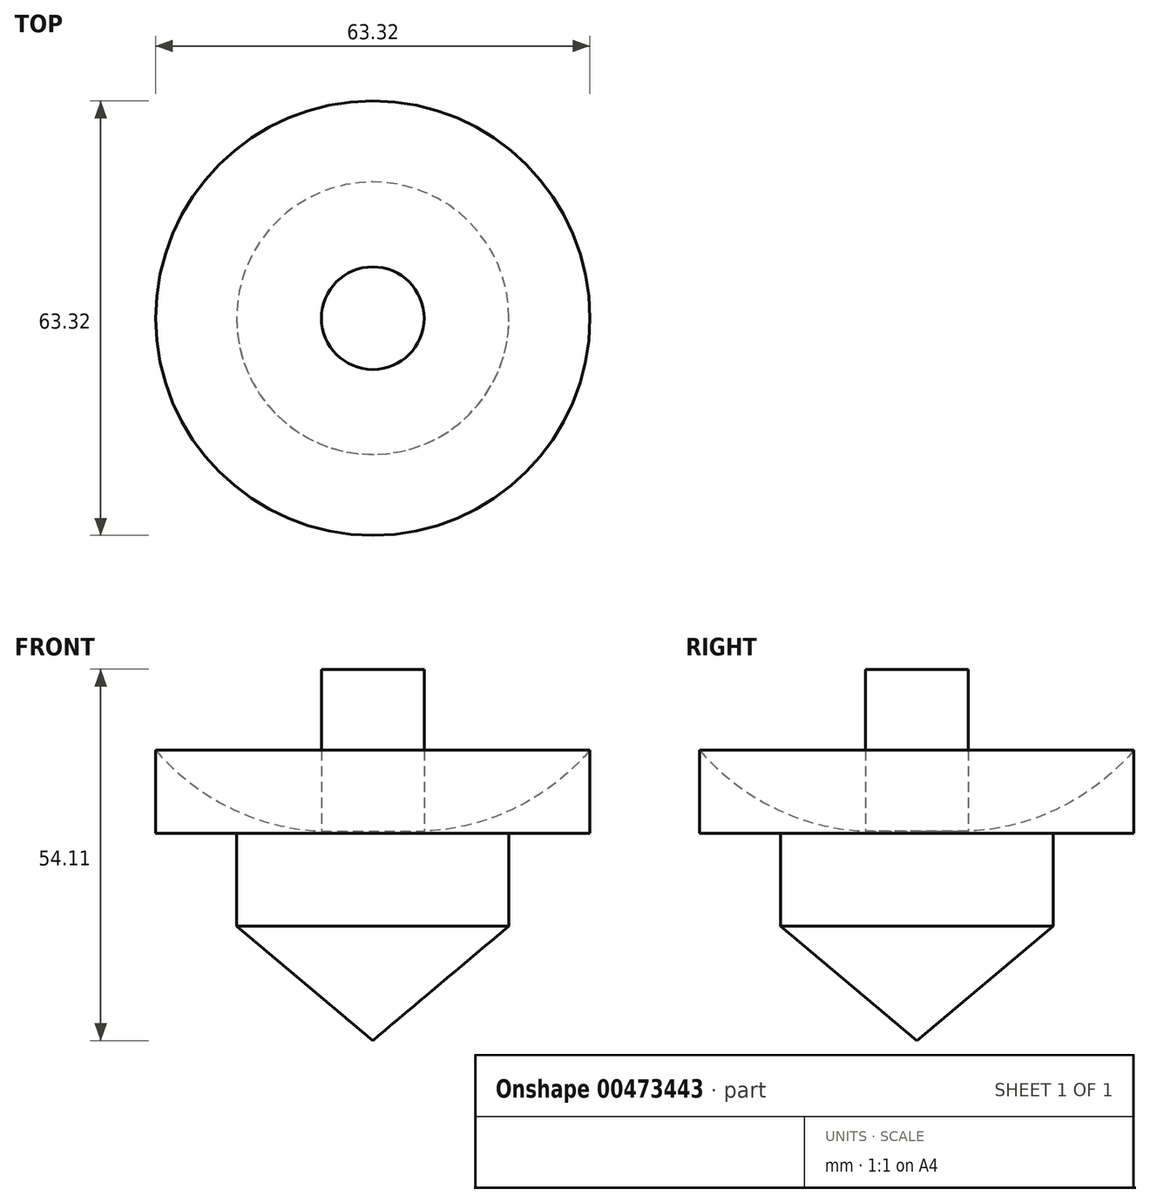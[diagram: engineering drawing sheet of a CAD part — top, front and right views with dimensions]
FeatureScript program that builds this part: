
annotation { "Feature Type Name" : "Feature", "Feature Type Description" : "" }
export const myFeature = defineFeature(function(context is Context, id is Id, definition is map)
    precondition{}
    {
        {
            var Q0;
            Q0=qCreatedBy(makeId("Front.planeOp"),FACE);
            var sketch = newSketch(context, id + "F0", { "sketchPlane" : qUnion([Q0])});
            skLineSegment(sketch, "E0", {"start": v(0, 0) * mm, "end": v(19.86, 16.7) * mm});
            skLineSegment(sketch, "E1", {"start": v(19.86, 16.7) * mm, "end": v(19.86, 30.22) * mm});
            skLineSegment(sketch, "E2", {"start": v(19.86, 30.22) * mm, "end": v(31.66, 30.22) * mm});
            skLineSegment(sketch, "E3", {"start": v(31.66, 30.22) * mm, "end": v(31.66, 42.3) * mm});
            skLineSegment(sketch, "E4", {"start": v(0, 0) * mm, "end": v(0, 54.1) * mm});
            skLineSegment(sketch, "E5", {"start": v(0, 54.1) * mm, "end": v(7.48, 54.1) * mm});
            skLineSegment(sketch, "E6", {"start": v(7.48, 54.1) * mm, "end": v(7.48, 30.5) * mm});
            skArc(sketch, "E7", {"start": v(7.48, 30.5) * mm, "mid": v(20.8, 33.9) * mm, "end": v(31.66, 42.3) * mm});
            skSolve(sketch);
        }
        {
            var Q0;
            Q0=makeQuery(id+"F0.imprint","IMPRINT",FACE,{"disambiguationData":[TD([[makeQuery(id+"F0.imprint","IMPRINT",EDGE,{"derivedFrom":sQuery(id+"F0.wireOp",EDGE,"E0")}),1.0]])]});
            var Q1;
            Q1=sQuery(id+"F0.wireOp",EDGE,"E4");
            revolve(context, id + "F1", {"entities" : qUnion([Q0]), "axis" : qUnion([Q1]), "revolveType" : RevolveType.FULL});
        }
    });
